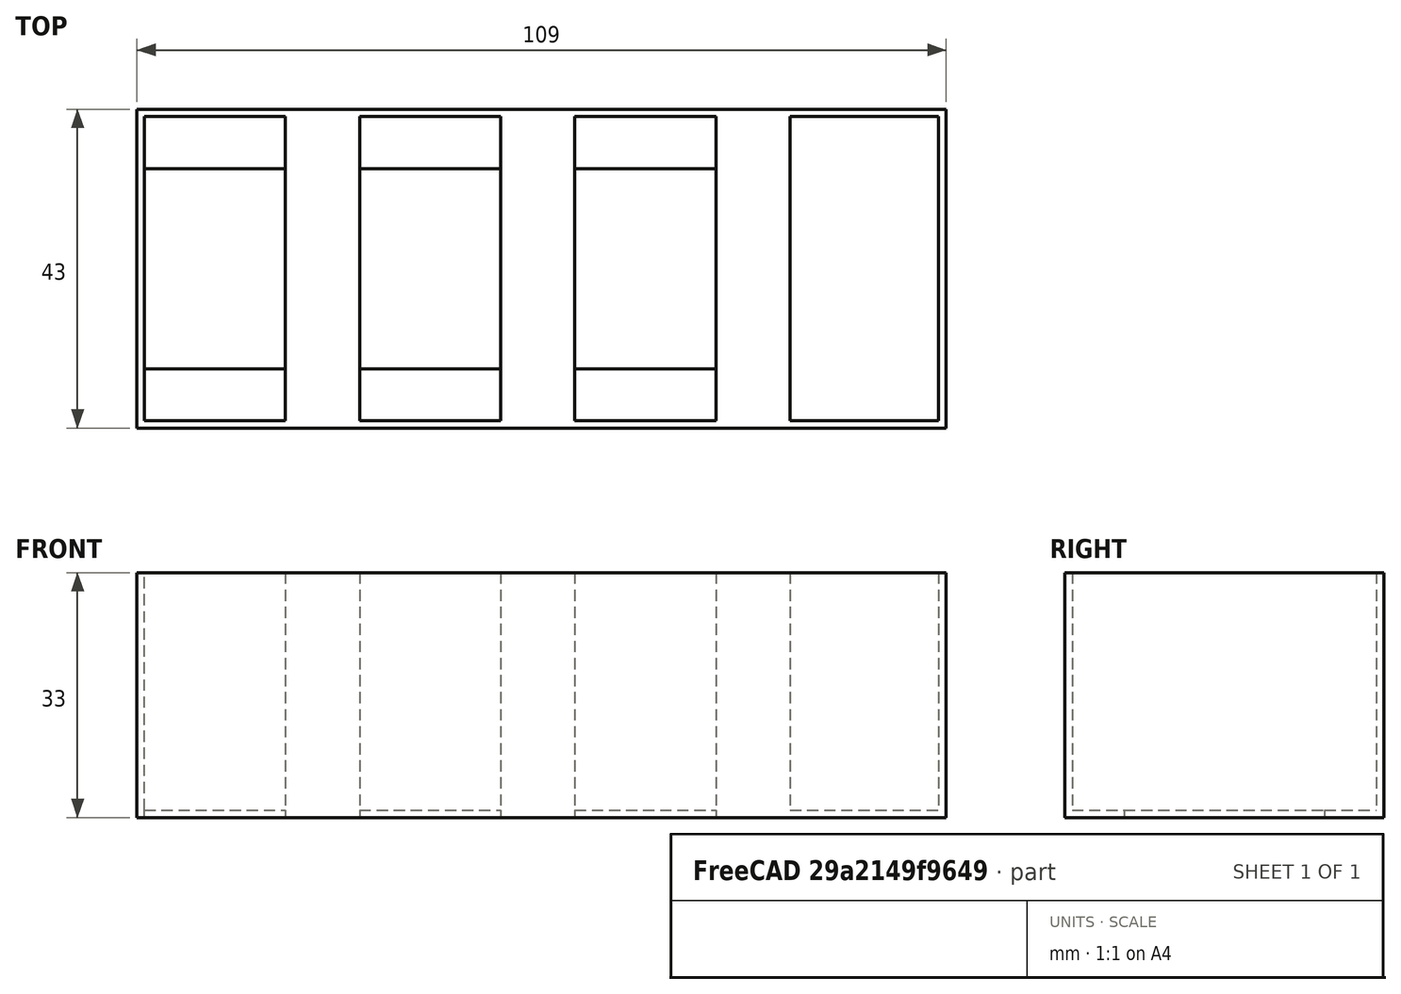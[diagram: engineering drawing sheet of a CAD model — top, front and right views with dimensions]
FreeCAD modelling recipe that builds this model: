
FCSTD DOCUMENT  (FreeCAD 0.18R4 (GitTag))
Label: dragons
License: All rights reserved
LicenseURL: http://en.wikipedia.org/wiki/All_rights_reserved
objects: Part::Box×12, Part::Cut×3, Part::MultiFuse×3
note: 18 computed .brp shape members not serialized (recipe doc carries the construction recipe); baked Part::Feature solids carry a one-line shape summary decoded from their .brp

FEATURE [Part::Box] Box  label="Cube"
  AttacherType = Attacher::AttachEngine3D
  Height = 33
  Length = 202
  Width = 43
FEATURE [Part::Box] Box001  label="Cube001"
  AttacherType = Attacher::AttachEngine3D
  Height = 33
  Length = 200
  Placement = pos=(1,1,0) rot=(0,0,1;0rad)
  Width = 41
FEATURE [Part::Cut] Cut
  Base = -> Box
  Tool = -> Box001
FEATURE [Part::Box] Box002  label="Cube002"
  AttacherType = Attacher::AttachEngine3D
  Height = 1
  Length = 202
  Width = 8
FEATURE [Part::Box] Box003  label="Cube003"
  AttacherType = Attacher::AttachEngine3D
  Height = 1
  Length = 202
  Placement = pos=(0,35,0) rot=(0,0,1;0rad)
  Width = 8
FEATURE [Part::MultiFuse] Fusion
  Shapes = -> [Cut,Box002,Box003]
FEATURE [Part::Box] Box004  label="Cube004"
  AttacherType = Attacher::AttachEngine3D
  Height = 33
  Length = 10
  Placement = pos=(20,0,0) rot=(0,0,1;0rad)
  Width = 43
FEATURE [Part::Box] Box005  label="Cube005"
  AttacherType = Attacher::AttachEngine3D
  Height = 33
  Length = 10
  Placement = pos=(49,0,0) rot=(0,0,1;0rad)
  Width = 43
FEATURE [Part::Box] Box006  label="Cube006"
  AttacherType = Attacher::AttachEngine3D
  Height = 33
  Length = 10
  Placement = pos=(78,0,0) rot=(0,0,1;0rad)
  Width = 43
FEATURE [Part::Box] Box007  label="Cube007"
  AttacherType = Attacher::AttachEngine3D
  Height = 33
  Length = 10
  Placement = pos=(108,0,0) rot=(0,0,1;0rad)
  Width = 43
FEATURE [Part::Box] Box008  label="Cube008"
  AttacherType = Attacher::AttachEngine3D
  Height = 33
  Length = 10
  Placement = pos=(168,0,0) rot=(0,0,1;0rad)
  Width = 43
FEATURE [Part::Box] Box009  label="Cube009"
  AttacherType = Attacher::AttachEngine3D
  Height = 33
  Length = 33
  Placement = pos=(169,0,0) rot=(0,0,1;0rad)
  Width = 43
FEATURE [Part::MultiFuse] Fusion001
  Shapes = -> [Fusion,Box004,Box006,Box005,Box008,Box007]
FEATURE [Part::Cut] Cut001
  Base = -> Fusion001
  Tool = -> Box009
FEATURE [Part::Box] Box010  label="Cube010"
  AttacherType = Attacher::AttachEngine3D
  Height = 1
  Length = 81
  Placement = pos=(88,0,0) rot=(0,0,1;0rad)
  Width = 43
FEATURE [Part::MultiFuse] Fusion002
  Shapes = -> [Box010,Cut001]
FEATURE [Part::Box] Box011  label="Cube011"
  AttacherType = Attacher::AttachEngine3D
  Height = 33
  Length = 60
  Placement = pos=(109,0,0) rot=(0,0,1;0rad)
  Width = 43
FEATURE [Part::Cut] Cut002
  Base = -> Fusion002
  Tool = -> Box011
